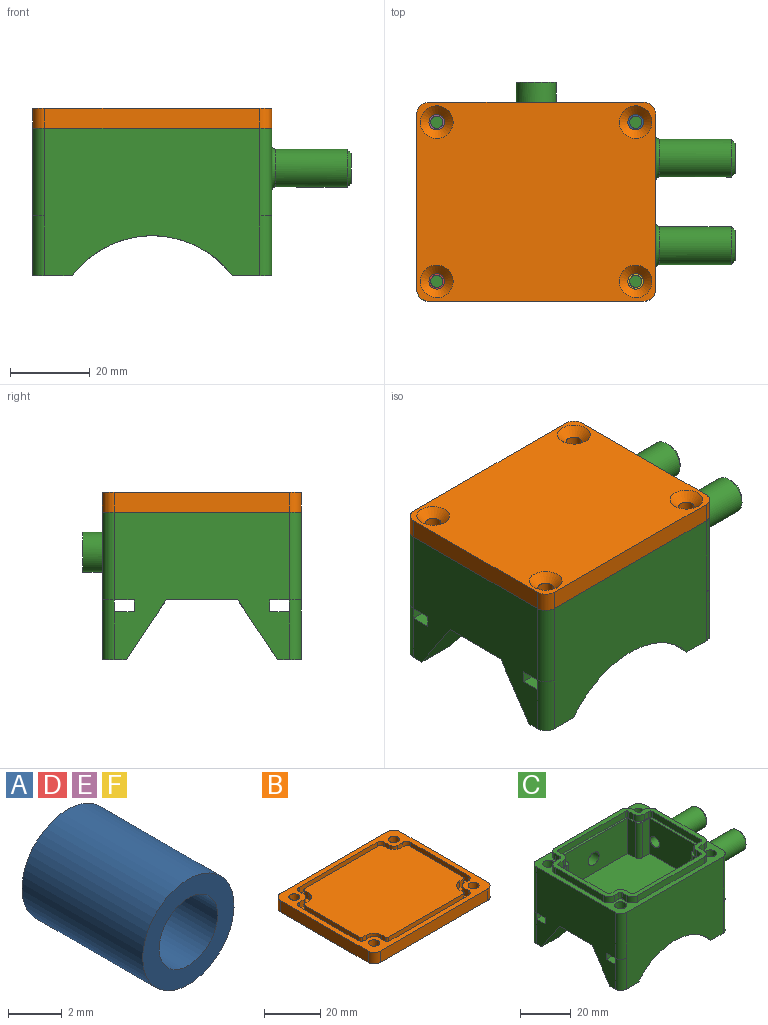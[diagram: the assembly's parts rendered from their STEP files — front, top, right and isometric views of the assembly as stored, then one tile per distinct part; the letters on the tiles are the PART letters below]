
ASSEMBLY  parts=6 mates=5
PART A: 4 faces, bbox 4.8x6.4x4.8 mm
  f0: plane 4.8x4.8mm, normal (0,1,0), area 10.6mm2, adj f2,f3
  f1: plane 4.8x4.8mm, normal (0,-1,0), area 10.6mm2, adj f2,f3
  f2: cylinder r=2.4mm len=6.35mm, axis (0,-1,0), area 95.8mm2, adj f0,f1
  f3: cylinder r=1.54mm len=6.35mm, axis (0,-1,0), area 61.4mm2, adj f0,f1
PART B: 68 faces, bbox 60x50x5 mm
  f0: plane 60x50mm, normal (0,0,-1), area 2781mm2, adj f2,f3,f4,f5,f6,f7,f8,f9
  f1: plane 60x50mm, normal (0,0,1), area 540.9mm2, adj f2,f3,f4,f5,f6,f7,f8,f9
  f2: cylinder r=3mm len=5mm, axis (0,0,-1), area 23.6mm2, adj f0,f1,f3,f9
  f3: plane 44x5mm, normal (-1,0,0), area 220mm2, adj f0,f1,f2,f4
  f4: cylinder r=3mm len=5mm, axis (0,0,-1), area 23.6mm2, adj f0,f1,f3,f5
  f5: plane 54x5mm, normal (0,-1,0), area 270mm2, adj f0,f1,f4,f6
  f6: cylinder r=3mm len=5mm, axis (0,0,-1), area 23.6mm2, adj f0,f1,f5,f7
  f7: plane 44x5mm, normal (1,0,0), area 220mm2, adj f0,f1,f6,f8
  f8: cylinder r=3mm len=5mm, axis (0,0,-1), area 23.6mm2, adj f0,f1,f7,f9
  f9: plane 54x5mm, normal (0,1,0), area 270mm2, adj f0,f1,f2,f8
  f10: cylinder r=2mm len=3mm, axis (0,0,1), area 9.4mm2, adj f1,f11,f33,f66
  f11: plane 29x3mm, normal (-1,0,0), area 87mm2, adj f1,f10,f12,f66
  f12: cylinder r=2mm len=3mm, axis (0,0,1), area 9.4mm2, adj f1,f11,f13,f66
  f13: plane 3x2.5mm, normal (0,1,0), area 7.5mm2, adj f1,f12,f14,f66
  f14: cylinder r=2mm len=3mm, axis (0,0,1), area 9.4mm2, adj f1,f13,f15,f66
  f15: plane 3x2.5mm, normal (-1,0,0), area 7.5mm2, adj f1,f14,f16,f66
  f16: cylinder r=2mm len=3mm, axis (0,0,1), area 9.4mm2, adj f1,f15,f17,f66
  f17: plane 39x3mm, normal (0,1,0), area 117mm2, adj f1,f16,f18,f66
  f18: cylinder r=2mm len=3mm, axis (0,0,1), area 9.4mm2, adj f1,f17,f19,f66
  f19: plane 3x2.5mm, normal (1,0,0), area 7.5mm2, adj f1,f18,f20,f66
  f20: cylinder r=2mm len=3mm, axis (0,0,1), area 9.4mm2, adj f1,f19,f21,f66
  f21: plane 3x2.5mm, normal (0,1,0), area 7.5mm2, adj f1,f20,f22,f66
  f22: cylinder r=2mm len=3mm, axis (0,0,1), area 9.4mm2, adj f1,f21,f23,f66
  f23: plane 29x3mm, normal (1,0,0), area 87mm2, adj f1,f22,f24,f66
  f24: cylinder r=2mm len=3mm, axis (0,0,1), area 9.4mm2, adj f1,f23,f25,f66
  f25: plane 3x2.5mm, normal (0,-1,0), area 7.5mm2, adj f1,f24,f26,f66
  f26: cylinder r=2mm len=3mm, axis (0,0,1), area 9.4mm2, adj f1,f25,f27,f66
  f27: plane 3x2.5mm, normal (1,0,0), area 7.5mm2, adj f1,f26,f28,f66
  f28: cylinder r=2mm len=3mm, axis (0,0,1), area 9.4mm2, adj f1,f27,f29,f66
  f29: plane 39x3mm, normal (0,-1,0), area 117mm2, adj f1,f28,f30,f66
  f30: cylinder r=2mm len=3mm, axis (0,0,1), area 9.4mm2, adj f1,f29,f31,f66
  f31: plane 3x2.5mm, normal (-1,0,0), area 7.5mm2, adj f1,f30,f32,f66
  f32: cylinder r=2mm len=3mm, axis (0,0,1), area 9.4mm2, adj f1,f31,f33,f66
  f33: plane 3x2.5mm, normal (0,-1,0), area 7.5mm2, adj f1,f10,f32,f66
  f34: cylinder r=1.95mm len=3.9mm, axis (0,0,-1), area 34.9mm2, adj f1,f35
  f35: cone r=4.1mm half-angle=45deg, axis (0,0,-1), area 57.8mm2, adj f0,f34
  f36: cylinder r=1.95mm len=3.9mm, axis (0,0,-1), area 34.9mm2, adj f1,f37
  f37: cone r=4.1mm half-angle=45deg, axis (0,0,-1), area 57.8mm2, adj f0,f36
  f38: cylinder r=1.95mm len=3.9mm, axis (0,0,-1), area 34.9mm2, adj f1,f39
  f39: cone r=4.1mm half-angle=45deg, axis (0,0,-1), area 57.8mm2, adj f0,f38
  f40: cylinder r=1.95mm len=3.9mm, axis (0,0,-1), area 34.9mm2, adj f1,f41
  f41: cone r=4.1mm half-angle=45deg, axis (0,0,-1), area 57.8mm2, adj f0,f40
  f42: cylinder r=0.71mm len=3mm, axis (0,0,1), area 3.4mm2, adj f43,f65,f66,f67
  f43: plane 3x1.85mm, normal (0,-1,0), area 5.5mm2, adj f42,f44,f66,f67
  f44: cylinder r=3.94mm len=3.94mm, axis (0,0,1), area 18.6mm2, adj f43,f45,f66,f67
  f45: plane 3x1.85mm, normal (1,0,0), area 5.5mm2, adj f44,f46,f66,f67
  f46: cylinder r=0.71mm len=3mm, axis (0,0,1), area 3.4mm2, adj f45,f47,f66,f67
  f47: plane 37.69x3mm, normal (0,-1,0), area 113.1mm2, adj f46,f48,f66,f67
  f48: cylinder r=0.71mm len=3mm, axis (0,0,1), area 3.4mm2, adj f47,f49,f66,f67
  f49: plane 3x1.85mm, normal (-1,0,0), area 5.5mm2, adj f48,f50,f66,f67
  f50: cylinder r=3.94mm len=3.94mm, axis (0,0,1), area 18.6mm2, adj f49,f51,f66,f67
  f51: plane 3x1.85mm, normal (0,-1,0), area 5.5mm2, adj f50,f52,f66,f67
  f52: cylinder r=0.71mm len=3mm, axis (0,0,1), area 3.4mm2, adj f51,f53,f66,f67
  f53: plane 27.69x3mm, normal (-1,0,0), area 83.1mm2, adj f52,f54,f66,f67
  f54: cylinder r=0.71mm len=3mm, axis (0,0,1), area 3.4mm2, adj f53,f55,f66,f67
  f55: plane 3x1.85mm, normal (0,1,0), area 5.5mm2, adj f54,f56,f66,f67
  f56: cylinder r=3.94mm len=3.94mm, axis (0,0,1), area 18.6mm2, adj f55,f57,f66,f67
  f57: plane 3x1.85mm, normal (-1,0,0), area 5.5mm2, adj f56,f58,f66,f67
  f58: cylinder r=0.71mm len=3mm, axis (0,0,1), area 3.4mm2, adj f57,f59,f66,f67
  f59: plane 37.69x3mm, normal (0,1,0), area 113.1mm2, adj f58,f60,f66,f67
  f60: cylinder r=0.71mm len=3mm, axis (0,0,1), area 3.4mm2, adj f59,f61,f66,f67
  f61: plane 3x1.85mm, normal (1,0,0), area 5.5mm2, adj f60,f62,f66,f67
  f62: cylinder r=3.94mm len=3.94mm, axis (0,0,1), area 18.6mm2, adj f61,f63,f66,f67
  f63: plane 3x1.85mm, normal (0,1,0), area 5.5mm2, adj f62,f64,f66,f67
  f64: cylinder r=0.71mm len=3mm, axis (0,0,1), area 3.4mm2, adj f63,f65,f66,f67
  f65: plane 27.69x3mm, normal (1,0,0), area 83.1mm2, adj f42,f64,f66,f67
  f66: plane 56x46mm, normal (0,0,1), area 364.8mm2, adj f10,f11,f12,f13,f14,f15,f16,f17
  f67: plane 52.12x42.12mm, normal (0,0,1), area 2038.8mm2, adj f42,f43,f44,f45,f46,f47,f48,f49
PART C: 122 faces, bbox 80x55x40 mm
  f0: plane 52x42mm, normal (0,0,1), area 161.6mm2, adj f6,f7,f8,f9,f50,f51,f52,f53
  f1: cylinder r=3.01mm len=6.7mm, axis (0,1,0), area 126.7mm2, adj f7,f94
  f2: plane 60x50mm, normal (0,0,1), area 527.5mm2, adj f12,f13,f14,f15,f16,f17,f18,f19
  f3: plane 9.88x6mm, normal (0,0,-1), area 57.3mm2, adj f12,f15,f32,f36,f41
  f4: plane 9.88x6mm, normal (0,0,-1), area 57.3mm2, adj f12,f13,f35,f39,f40
  f5: plane 60x18mm, normal (0,0,-1), area 1080mm2, adj f12,f14,f32,f35
  f6: plane 28x17mm, normal (-1,0,0), area 436.7mm2, adj f0,f10,f11,f26,f50,f53
  f7: plane 38x17mm, normal (0,-1,0), area 617.5mm2, adj f0,f1,f10,f52,f60
  f8: plane 28x17mm, normal (1,0,0), area 476mm2, adj f0,f10,f57,f59
  f9: plane 38x17mm, normal (0,1,0), area 646mm2, adj f0,f10,f54,f56
  f10: plane 50x40mm, normal (0,0,1), area 1859.4mm2, adj f6,f7,f8,f9,f50,f51,f52,f53
  f11: cylinder r=2.5mm len=25mm, axis (1,0,0), area 392.7mm2, adj f6,f21
  f12: plane 44x37mm, normal (1,0,0), area 970.3mm2, adj f2,f3,f4,f5,f17,f19,f23,f27
  f13: plane 54x37mm, normal (0,1,0), area 1638.3mm2, adj f2,f4,f18,f19,f29,f34,f38,f39
  f14: plane 44x37mm, normal (-1,0,0), area 1178mm2, adj f2,f5,f16,f18,f32,f33,f34,f35
  f15: plane 54x37mm, normal (0,-1,0), area 1716.9mm2, adj f2,f3,f16,f17,f33,f36,f37,f41
  f16: cylinder r=3mm len=22mm, axis (0,0,-1), area 103.7mm2, adj f2,f14,f15,f37
  f17: cylinder r=3mm len=22mm, axis (0,0,-1), area 103.7mm2, adj f2,f12,f15,f36
  f18: cylinder r=3mm len=22mm, axis (0,0,-1), area 103.7mm2, adj f2,f13,f14,f38
  f19: cylinder r=3mm len=22mm, axis (0,0,-1), area 103.7mm2, adj f2,f12,f13,f39
  f20: cylinder r=4.75mm len=18mm, axis (-1,0,0), area 537.2mm2, adj f22,f23
  f21: plane 7.5x7.5mm, normal (1,0,0), area 24.5mm2, adj f11,f22
  f22: cone r=3.75mm half-angle=45deg, axis (-1,0,0), area 37.8mm2, adj f20,f21
  f23: torus R=5.75mm, axis (-1,0,0), area 50.5mm2, adj f12,f20
  f24: cylinder r=4.75mm len=18mm, axis (-1,0,0), area 537.2mm2, adj f27,f28
  f25: plane 7.5x7.5mm, normal (1,0,0), area 24.5mm2, adj f26,f28
  f26: cylinder r=2.5mm len=25mm, axis (1,0,0), area 392.7mm2, adj f6,f25
  f27: torus R=5.75mm, axis (-1,0,0), area 50.5mm2, adj f12,f24
  f28: cone r=4.75mm half-angle=45deg, axis (-1,0,0), area 37.8mm2, adj f24,f25
  f29: cylinder r=5mm len=10mm, axis (0,-1,0), area 157.1mm2, adj f13,f30
  f30: plane 10x10mm, normal (0,1,0), area 50.1mm2, adj f29,f31
  f31: cylinder r=3.01mm len=6.02mm, axis (0,1,0), area 32.2mm2, adj f30,f95
  f32: plane 60x15mm, normal (0,0.83,-0.55), area 743.8mm2, adj f3,f5,f12,f14,f33,f41
  f33: plane 9.88x6mm, normal (0,0,-1), area 57.3mm2, adj f14,f15,f32,f37,f41
  f34: plane 9.88x6mm, normal (0,0,-1), area 57.3mm2, adj f13,f14,f35,f38,f40
  f35: plane 60x15mm, normal (0,-0.83,-0.55), area 743.8mm2, adj f4,f5,f12,f14,f34,f40
  f36: cylinder r=3mm len=15mm, axis (0,0,1), area 70.7mm2, adj f3,f12,f15,f17,f49
  f37: cylinder r=3mm len=15mm, axis (0,0,1), area 70.7mm2, adj f14,f15,f16,f33,f49
  f38: cylinder r=3mm len=15mm, axis (0,0,-1), area 70.7mm2, adj f13,f14,f18,f34,f45
  f39: cylinder r=3mm len=15mm, axis (0,0,-1), area 70.7mm2, adj f4,f12,f13,f19,f45
  f40: cylinder r=25.25mm len=40.25mm, axis (0,1,0), area 483.5mm2, adj f4,f13,f34,f35
  f41: cylinder r=25.25mm len=40.25mm, axis (0,1,0), area 483.5mm2, adj f3,f15,f32,f33
  f42: plane 60x5mm, normal (0,0,1), area 300mm2, adj f12,f14,f43,f45
  f43: plane 60x3mm, normal (0,1,0), area 180mm2, adj f12,f14,f42,f44
  f44: plane 60x5mm, normal (0,0,-1), area 300mm2, adj f12,f14,f43,f45
  f45: plane 60x3mm, normal (0,-1,0), area 180mm2, adj f38,f39,f42,f44
  f46: plane 60x5mm, normal (0,0,-1), area 300mm2, adj f12,f14,f47,f49
  f47: plane 60x3mm, normal (0,-1,0), area 180mm2, adj f12,f14,f46,f48
  f48: plane 60x5mm, normal (0,0,1), area 300mm2, adj f12,f14,f47,f49
  f49: plane 60x3mm, normal (0,1,0), area 180mm2, adj f36,f37,f46,f48
  f50: plane 17x4mm, normal (0,-1,0), area 68mm2, adj f0,f6,f10,f51
  f51: cylinder r=2mm len=17mm, axis (0,0,1), area 53.4mm2, adj f0,f10,f50,f52
  f52: plane 17x4mm, normal (-1,0,0), area 68mm2, adj f0,f7,f10,f51
  f53: plane 17x4mm, normal (0,1,0), area 68mm2, adj f0,f6,f10,f55
  f54: plane 17x4mm, normal (-1,0,0), area 68mm2, adj f0,f9,f10,f55
  f55: cylinder r=2mm len=17mm, axis (0,0,1), area 53.4mm2, adj f0,f10,f53,f54
  f56: plane 17x4mm, normal (1,0,0), area 68mm2, adj f0,f9,f10,f58
  f57: plane 17x4mm, normal (0,1,0), area 68mm2, adj f0,f8,f10,f58
  f58: cylinder r=2mm len=17mm, axis (0,0,1), area 53.4mm2, adj f0,f10,f56,f57
  f59: plane 17x4mm, normal (0,-1,0), area 68mm2, adj f0,f8,f10,f61
  f60: plane 17x4mm, normal (1,0,0), area 68mm2, adj f0,f7,f10,f61
  f61: cylinder r=2mm len=17mm, axis (0,0,1), area 53.4mm2, adj f0,f10,f59,f60
  f62: cylinder r=2.4mm len=6.4mm, axis (0,0,1), area 96.5mm2, adj f2,f63
  f63: plane 4.8x4.8mm, normal (0,0,1), area 18.1mm2, adj f62
  f64: cylinder r=2.4mm len=6.4mm, axis (0,0,1), area 96.5mm2, adj f2,f65
  f65: plane 4.8x4.8mm, normal (0,0,1), area 18.1mm2, adj f64
  f66: cylinder r=2.4mm len=6.4mm, axis (0,0,1), area 96.5mm2, adj f2,f67
  f67: plane 4.8x4.8mm, normal (0,0,1), area 18.1mm2, adj f66
  f68: cylinder r=2.4mm len=6.4mm, axis (0,0,1), area 96.5mm2, adj f2,f69
  f69: plane 4.8x4.8mm, normal (0,0,1), area 18.1mm2, adj f68
  f70: cylinder r=3mm len=3mm, axis (0,0,-1), area 14.1mm2, adj f2,f71,f93,f121
  f71: plane 37x3mm, normal (0,1,0), area 111mm2, adj f2,f70,f72,f121
  f72: cylinder r=3mm len=3mm, axis (0,0,-1), area 14.1mm2, adj f2,f71,f73,f121
  f73: plane 3x2.5mm, normal (-1,0,0), area 7.5mm2, adj f2,f72,f74,f121
  f74: cylinder r=1mm len=3mm, axis (0,0,-1), area 4.7mm2, adj f2,f73,f75,f121
  f75: plane 3x2.5mm, normal (0,1,0), area 7.5mm2, adj f2,f74,f76,f121
  f76: cylinder r=3mm len=3mm, axis (0,0,-1), area 14.1mm2, adj f2,f75,f77,f121
  f77: plane 27x3mm, normal (-1,0,0), area 81mm2, adj f2,f76,f78,f121
  f78: cylinder r=3mm len=3mm, axis (0,0,-1), area 14.1mm2, adj f2,f77,f79,f121
  f79: plane 3x2.5mm, normal (0,-1,0), area 7.5mm2, adj f2,f78,f80,f121
  f80: cylinder r=1mm len=3mm, axis (0,0,-1), area 4.7mm2, adj f2,f79,f81,f121
  f81: plane 3x2.5mm, normal (-1,0,0), area 7.5mm2, adj f2,f80,f82,f121
  f82: cylinder r=3mm len=3mm, axis (0,0,-1), area 14.1mm2, adj f2,f81,f83,f121
  f83: plane 37x3mm, normal (0,-1,0), area 111mm2, adj f2,f82,f84,f121
  f84: cylinder r=3mm len=3mm, axis (0,0,-1), area 14.1mm2, adj f2,f83,f85,f121
  f85: plane 3x2.5mm, normal (1,0,0), area 7.5mm2, adj f2,f84,f86,f121
  f86: cylinder r=1mm len=3mm, axis (0,0,-1), area 4.7mm2, adj f2,f85,f87,f121
  f87: plane 3x2.5mm, normal (0,-1,0), area 7.5mm2, adj f2,f86,f88,f121
  f88: cylinder r=3mm len=3mm, axis (0,0,-1), area 14.1mm2, adj f2,f87,f89,f121
  f89: plane 27x3mm, normal (1,0,0), area 81mm2, adj f2,f88,f90,f121
  f90: cylinder r=3mm len=3mm, axis (0,0,-1), area 14.1mm2, adj f2,f89,f91,f121
  f91: plane 3x2.5mm, normal (0,1,0), area 7.5mm2, adj f2,f90,f92,f121
  f92: cylinder r=1mm len=3mm, axis (0,0,-1), area 4.7mm2, adj f2,f91,f93,f121
  f93: plane 3x2.5mm, normal (1,0,0), area 7.5mm2, adj f2,f70,f92,f121
  f94: plane 8.37x8.37mm, normal (0,1,0), area 26.6mm2, adj f1,f96
  f95: plane 8.37x8.37mm, normal (0,-1,0), area 26.6mm2, adj f31,f96
  f96: cylinder r=4.19mm len=8.37mm, axis (0,1,0), area 42.1mm2, adj f94,f95
  f97: plane 27x3mm, normal (1,0,0), area 81mm2, adj f0,f98,f120,f121
  f98: cylinder r=1mm len=3mm, axis (0,0,-1), area 4.7mm2, adj f0,f97,f99,f121
  f99: plane 3x2.5mm, normal (0,-1,0), area 7.5mm2, adj f0,f98,f100,f121
  f100: cylinder r=3mm len=3mm, axis (0,0,-1), area 14.1mm2, adj f0,f99,f101,f121
  f101: plane 3x2.5mm, normal (1,0,0), area 7.5mm2, adj f0,f100,f102,f121
  f102: cylinder r=1mm len=3mm, axis (0,0,-1), area 4.7mm2, adj f0,f101,f103,f121
  f103: plane 37x3mm, normal (0,-1,0), area 111mm2, adj f0,f102,f104,f121
  f104: cylinder r=1mm len=3mm, axis (0,0,-1), area 4.7mm2, adj f0,f103,f105,f121
  f105: plane 3x2.5mm, normal (-1,0,0), area 7.5mm2, adj f0,f104,f106,f121
  f106: cylinder r=3mm len=3mm, axis (0,0,-1), area 14.1mm2, adj f0,f105,f107,f121
  f107: plane 3x2.5mm, normal (0,-1,0), area 7.5mm2, adj f0,f106,f108,f121
  f108: cylinder r=1mm len=3mm, axis (0,0,-1), area 4.7mm2, adj f0,f107,f109,f121
  f109: plane 27x3mm, normal (-1,0,0), area 81mm2, adj f0,f108,f110,f121
  f110: cylinder r=1mm len=3mm, axis (0,0,-1), area 4.7mm2, adj f0,f109,f111,f121
  f111: plane 3x2.5mm, normal (0,1,0), area 7.5mm2, adj f0,f110,f112,f121
  f112: cylinder r=3mm len=3mm, axis (0,0,-1), area 14.1mm2, adj f0,f111,f113,f121
  f113: plane 3x2.5mm, normal (-1,0,0), area 7.5mm2, adj f0,f112,f114,f121
  f114: cylinder r=1mm len=3mm, axis (0,0,-1), area 4.7mm2, adj f0,f113,f115,f121
  f115: plane 37x3mm, normal (0,1,0), area 111mm2, adj f0,f114,f116,f121
  f116: cylinder r=1mm len=3mm, axis (0,0,-1), area 4.7mm2, adj f0,f115,f117,f121
  f117: plane 3x2.5mm, normal (1,0,0), area 7.5mm2, adj f0,f116,f118,f121
  f118: cylinder r=3mm len=3mm, axis (0,0,-1), area 14.1mm2, adj f0,f117,f119,f121
  f119: plane 3x2.5mm, normal (0,1,0), area 7.5mm2, adj f0,f118,f120,f121
  f120: cylinder r=1mm len=3mm, axis (0,0,-1), area 4.7mm2, adj f0,f97,f119,f121
  f121: plane 56x46mm, normal (0,0,1), area 371.4mm2, adj f70,f71,f72,f73,f74,f75,f76,f77
PART D: same geometry as A
PART E: same geometry as A
PART F: same geometry as A
PLACE A rot(axis=(-1,0,0),90deg) t=(23.62,25.16,21.03)mm
PLACE B rot(axis=(-1,0,0),180deg) t=(-1.38,5.16,26.03)mm
PLACE C t=(-1.38,5.16,-0.97)mm fixed
PLACE D rot(axis=(-1,0,0),90deg) t=(-26.38,-14.84,21.03)mm
PLACE E rot(axis=(-1,0,0),90deg) t=(-26.38,25.16,21.03)mm
PLACE F rot(axis=(-1,0,0),90deg) t=(23.62,-14.84,21.03)mm
MATE fastened E.f2 <-> C.f64  axis (0,0,1) through (-26.38,25.16,21.03)mm
MATE fastened C.f68 <-> F.f2  axis (0,0,1) through (23.62,-14.84,21.03)mm
MATE fastened A.f2 <-> C.f62  axis (0,0,1) through (23.62,25.16,21.03)mm
MATE fastened D.f2 <-> C.f66  axis (0,0,1) through (-26.38,-14.84,21.03)mm
MATE fastened B.f38 <-> C.f62  axis (0,0,-1) through (23.62,25.16,21.03)mm
